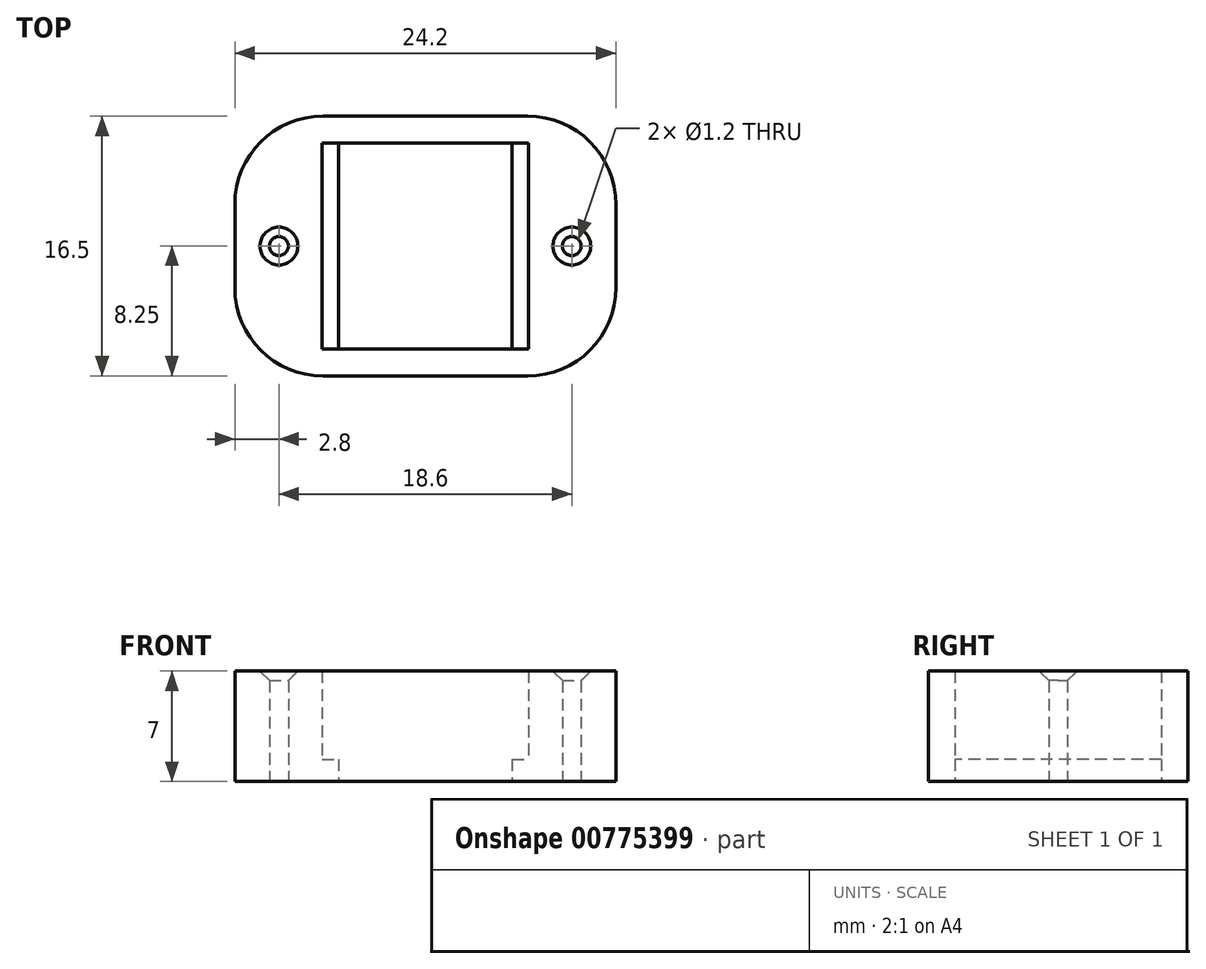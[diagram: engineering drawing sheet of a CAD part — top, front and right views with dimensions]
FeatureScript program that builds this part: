
annotation { "Feature Type Name" : "Feature", "Feature Type Description" : "" }
export const myFeature = defineFeature(function(context is Context, id is Id, definition is map)
    precondition{}
    {
        {
            var Q0;
            Q0=qCreatedBy(makeId("Top.planeOp"),FACE);
            var sketch = newSketch(context, id + "F0", { "sketchPlane" : qUnion([Q0])});
            skLineSegment(sketch, "E0.bottom", {"start": v(12.1, 8.25) * mm, "end": v(-12.1, 8.25) * mm});
            skLineSegment(sketch, "E0.top", {"start": v(12.1, -8.25) * mm, "end": v(-12.1, -8.25) * mm});
            skLineSegment(sketch, "E0.left", {"start": v(12.1, 8.25) * mm, "end": v(12.1, -8.25) * mm});
            skLineSegment(sketch, "E0.right", {"start": v(-12.1, 8.25) * mm, "end": v(-12.1, -8.25) * mm});
            skPoint(sketch, "E0.middle", {"position": v(0, 0) * mm});
            skSolve(sketch);
        }
        {
            var Q0;
            Q0=makeQuery(id+"F0.imprint","IMPRINT",FACE,{"disambiguationData":[TD([[makeQuery(id+"F0.imprint","IMPRINT",EDGE,{"derivedFrom":sQuery(id+"F0.wireOp",EDGE,"E0.bottom")}),1.0]])]});
            extrude(context, id + "F1", {"entities" : qUnion([Q0]), "depth" : (1.5 + 1.6 + 2.5 + 1.4) * mm, "offsetDistance" : 25 * mm});
        }
        {
            var Q0;
            Q0=makeQuery(id+"F1.opExtrude","SWEPT_EDGE",EDGE,{"disambiguationData":[OSD([sQuery(id+"F0.wireOp",EDGE,"E0.top"),sQuery(id+"F0.wireOp",EDGE,"E0.right")])]});
            var Q1;
            Q1=makeQuery(id+"F1.opExtrude","SWEPT_EDGE",EDGE,{"disambiguationData":[OSD([sQuery(id+"F0.wireOp",EDGE,"E0.top"),sQuery(id+"F0.wireOp",EDGE,"E0.left")])]});
            var Q2;
            Q2=makeQuery(id+"F1.opExtrude","SWEPT_EDGE",EDGE,{"disambiguationData":[OSD([sQuery(id+"F0.wireOp",EDGE,"E0.bottom"),sQuery(id+"F0.wireOp",EDGE,"E0.left")])]});
            var Q3;
            Q3=makeQuery(id+"F1.opExtrude","SWEPT_EDGE",EDGE,{"disambiguationData":[OSD([sQuery(id+"F0.wireOp",EDGE,"E0.bottom"),sQuery(id+"F0.wireOp",EDGE,"E0.right")])]});
            fillet(context, id + "F2", {"entities" : qUnion([Q0, Q1, Q2, Q3]), "radius" : 5.6 * mm, "tangentPropagation" : true, "allowEdgeOverflow" : false});
        }
        {
            var Q0;
            Q0=makeQuery(id+"F1.opExtrude","CAP_FACE",FACE,{"disambiguationData":[OSD([sQuery(id+"F0.wireOp",EDGE,"E0.bottom"),sQuery(id+"F0.wireOp",EDGE,"E0.top"),sQuery(id+"F0.wireOp",EDGE,"E0.left"),sQuery(id+"F0.wireOp",EDGE,"E0.right")])],"isStart":true});
            var sketch = newSketch(context, id + "F3", { "sketchPlane" : qUnion([Q0])});
            skLineSegment(sketch, "E1.bottom", {"start": v(-6.55, -6.55) * mm, "end": v(6.55, -6.55) * mm});
            skLineSegment(sketch, "E1.top", {"start": v(-6.55, 6.55) * mm, "end": v(6.55, 6.55) * mm});
            skLineSegment(sketch, "E1.left", {"start": v(-6.55, -6.55) * mm, "end": v(-6.55, 6.55) * mm});
            skLineSegment(sketch, "E1.right", {"start": v(6.55, -6.55) * mm, "end": v(6.55, 6.55) * mm});
            skPoint(sketch, "E1.middle", {"position": v(0, 0) * mm});
            skSolve(sketch);
        }
        {
            var Q0;
            Q0 = qSketchRegion(id + "F3", true);
            extrude(context, id + "F4", {"entities" : qUnion([Q0]), "operationType" : NewBodyOperationType.REMOVE, "endBound" : BoundingType.THROUGH_ALL, "oppositeDirection" : true, "depth" : 25 * mm, "offsetDistance" : 25 * mm});
        }
        {
            var Q0;
            Q0=makeQuery(id+"F1.opExtrude","CAP_FACE",FACE,{"disambiguationData":[OSD([sQuery(id+"F0.wireOp",EDGE,"E0.bottom"),sQuery(id+"F0.wireOp",EDGE,"E0.top"),sQuery(id+"F0.wireOp",EDGE,"E0.left"),sQuery(id+"F0.wireOp",EDGE,"E0.right")])],"isStart":true});
            var sketch = newSketch(context, id + "F5", { "sketchPlane" : qUnion([Q0])});
            skLineSegment(sketch, "E2", {"start": v(-6.55, 6.55) * mm, "end": v(-5.5, 6.55) * mm, "construction": true});
            skLineSegment(sketch, "E3", {"start": v(0, 6.55) * mm, "end": v(0, -6.55) * mm, "construction": true});
            skLineSegment(sketch, "E4.bottom", {"start": v(-5.5, 6.55) * mm, "end": v(-6.55, 6.55) * mm});
            skLineSegment(sketch, "E4.top", {"start": v(-5.5, -6.55) * mm, "end": v(-6.55, -6.55) * mm});
            skLineSegment(sketch, "E4.left", {"start": v(-5.5, 6.55) * mm, "end": v(-5.5, -6.55) * mm});
            skLineSegment(sketch, "E4.right", {"start": v(-6.55, 6.55) * mm, "end": v(-6.55, -6.55) * mm});
            skLineSegment(sketch, "E5.MirrorCS", {"start": v(5.5, 6.55) * mm, "end": v(6.55, 6.55) * mm});
            skLineSegment(sketch, "E6.MirrorCS", {"start": v(5.5, 6.55) * mm, "end": v(5.5, -6.55) * mm});
            skLineSegment(sketch, "E7.MirrorCS", {"start": v(5.5, -6.55) * mm, "end": v(6.55, -6.55) * mm});
            skLineSegment(sketch, "E8.MirrorCS", {"start": v(6.55, 6.55) * mm, "end": v(6.55, -6.55) * mm});
            skLineSegment(sketch, "E9.MirrorCS", {"start": v(6.55, 6.55) * mm, "end": v(5.5, 6.55) * mm, "construction": true});
            skSolve(sketch);
        }
        {
            var Q0;
            Q0 = qSketchRegion(id + "F5", true);
            extrude(context, id + "F6", {"entities" : qUnion([Q0]), "operationType" : NewBodyOperationType.ADD, "oppositeDirection" : true, "depth" : 1.4 * mm, "offsetDistance" : 25 * mm});
        }
        {
            var Q0;
            Q0=makeQuery(id+"F6.boolean.opBoolean","MERGE",FACE,{"derivedFrom":[makeQuery(id+"F1.opExtrude","CAP_FACE",FACE,{"disambiguationData":[OSD([sQuery(id+"F0.wireOp",EDGE,"E0.bottom"),sQuery(id+"F0.wireOp",EDGE,"E0.top"),sQuery(id+"F0.wireOp",EDGE,"E0.left"),sQuery(id+"F0.wireOp",EDGE,"E0.right")])],"isStart":true}),makeQuery(id+"F6.opExtrude","CAP_FACE",FACE,{"disambiguationData":[OSD([sQuery(id+"F5.wireOp",EDGE,"E4.bottom"),sQuery(id+"F5.wireOp",EDGE,"E4.top"),sQuery(id+"F5.wireOp",EDGE,"E4.left"),sQuery(id+"F5.wireOp",EDGE,"E4.right")])],"isStart":true}),makeQuery(id+"F6.opExtrude","CAP_FACE",FACE,{"disambiguationData":[OSD([sQuery(id+"F5.wireOp",EDGE,"E5.MirrorCS"),sQuery(id+"F5.wireOp",EDGE,"E6.MirrorCS"),sQuery(id+"F5.wireOp",EDGE,"E7.MirrorCS"),sQuery(id+"F5.wireOp",EDGE,"E8.MirrorCS")])],"isStart":true})]});
            var sketch = newSketch(context, id + "F7", { "sketchPlane" : qUnion([Q0])});
            skLineSegment(sketch, "E10", {"start": v(0, 6.55) * mm, "end": v(0, -6.55) * mm, "construction": true});
            skLineSegment(sketch, "E11", {"start": v(-12.1, 0) * mm, "end": v(-9.3, 0) * mm, "construction": true});
            skCircle(sketch, "E12", {"center": v(-9.3, 0) * mm, "radius": 0.6 * mm});
            skCircle(sketch, "E13.MirrorC", {"center": v(9.3, 0) * mm, "radius": 0.6 * mm});
            skSolve(sketch);
        }
        {
            var Q0;
            Q0 = qSketchRegion(id + "F7", true);
            extrude(context, id + "F8", {"entities" : qUnion([Q0]), "operationType" : NewBodyOperationType.REMOVE, "endBound" : BoundingType.THROUGH_ALL, "oppositeDirection" : true, "depth" : 25 * mm, "offsetDistance" : 25 * mm});
        }
        {
            var Q0;
            Q0=makeQuery(id+"F8.boolean.opBoolean","INTERSECT",EDGE,{"derivedFrom":[makeQuery(id+"F1.opExtrude","CAP_FACE",FACE,{"disambiguationData":[OSD([sQuery(id+"F0.wireOp",EDGE,"E0.bottom"),sQuery(id+"F0.wireOp",EDGE,"E0.top"),sQuery(id+"F0.wireOp",EDGE,"E0.left"),sQuery(id+"F0.wireOp",EDGE,"E0.right")])],"isStart":false}),makeQuery(id+"F8.opExtrude","SWEPT_FACE",FACE,{"disambiguationData":[OSD([sQuery(id+"F7.wireOp",EDGE,"E13.MirrorC")])]})]});
            var Q1;
            Q1=makeQuery(id+"F8.boolean.opBoolean","INTERSECT",EDGE,{"derivedFrom":[makeQuery(id+"F1.opExtrude","CAP_FACE",FACE,{"disambiguationData":[OSD([sQuery(id+"F0.wireOp",EDGE,"E0.bottom"),sQuery(id+"F0.wireOp",EDGE,"E0.top"),sQuery(id+"F0.wireOp",EDGE,"E0.left"),sQuery(id+"F0.wireOp",EDGE,"E0.right")])],"isStart":false}),makeQuery(id+"F8.opExtrude","SWEPT_FACE",FACE,{"disambiguationData":[OSD([sQuery(id+"F7.wireOp",EDGE,"E12")])]})]});
            chamfer(context, id + "F9", {"entities" : qUnion([Q0, Q1]), "width" : .6 * mm, "tangentPropagation" : true});
        }
    });
